# Revit family: MDCI-1 [8-10]
name_source: partatom
category: HLS-Bauteile
revit_build: Autodesk Revit 2017 (Build: 20160720_1515(x64)
units: mm (PartAtom-declared; Revit-internal decimal feet)

## family parameters
Arbeitsebenenbasiert = Nein
Beim Laden mit Abzugskörper schneiden = Nein
Bemaßung runder Anschluss = Durchmesser verwenden
Gemeinsam genutzt = Nein
Immer vertikal = Ja
OmniClass-Nummer = 23.75.00.00
OmniClass-Titel = Climate Control (HVAC)
Raumberechnungspunkt = Nein
Teiletyp = Normal

## types (2) — shared parameters
Air Flow max = 5500 m³/h
Beschreibung = High efficiency air cooled
Casing color = SB2014
Compressor = 1
Condensation = Air
Cooling Power Input = 2 kW
Depth = 396.000 mm
Gas = R410A
Gas pipe = 15.900 mm
Heating Power Input = 2 kW
Height = 966.000 mm
Hersteller = Bosch
Installation = Outdoor installation
Liquid pipe = 9.520 mm
Machine material = Galvanized Steel
Min cable selection (power wiring) = 5*4mm2
Net Weight = 75.50 kg
Power supply = 220-240 1N~50Hz
Series = mini VRF
Width = 1075.000 mm
clearance access behind = 300.000 mm
clearance access front = 2000.000 mm
clearance access left = 600.000 mm
clearance access right = 300.000 mm

## per-type parameters (varying)
| type | Cooling Capacity | Heating Capacity | Maximum Fuse Amps | Minimum Circuit Amps |
| MDCI8-1 | 7.200 kW | 7.200 kW | 25 A | 26 A |
| MDCI10-1 | 9.000 kW | 9.000 kW | 32 A | 28 A |

note: column(s) folded — value = type name in every type: Modell

## geometry (parser evidence)
native form markers: Sweep x3
no freeform markers — native parametric forms only
